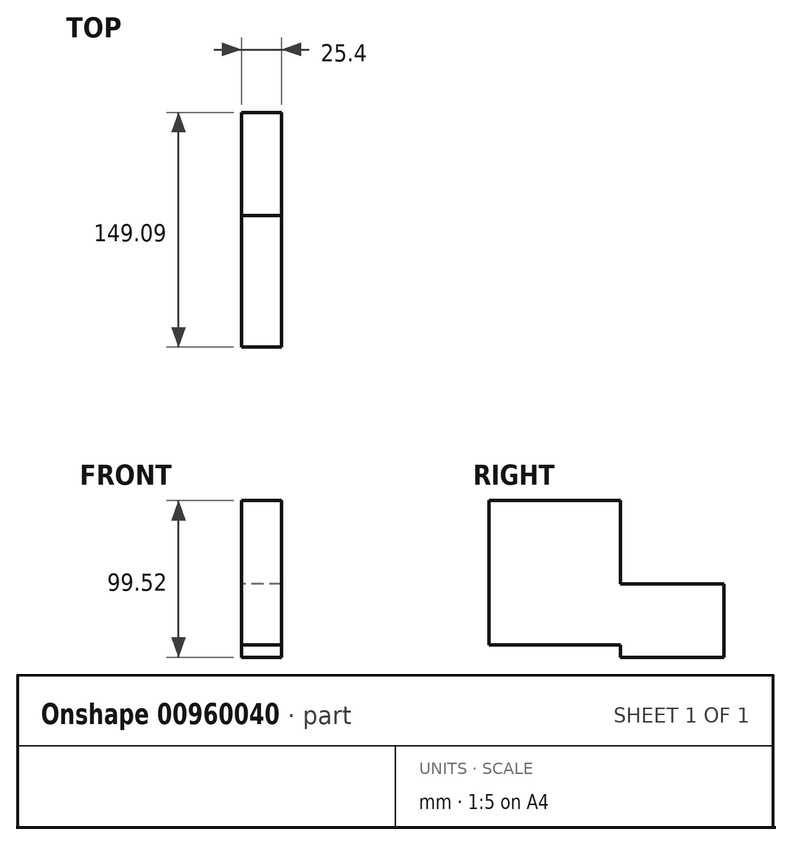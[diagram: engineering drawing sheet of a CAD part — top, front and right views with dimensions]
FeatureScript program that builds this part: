
annotation { "Feature Type Name" : "Feature", "Feature Type Description" : "" }
export const myFeature = defineFeature(function(context is Context, id is Id, definition is map)
    precondition{}
    {
        {
            var Q0;
            Q0=qCreatedBy(makeId("Right.planeOp"),FACE);
            var sketch = newSketch(context, id + "F0", { "sketchPlane" : qUnion([Q0])});
            skLineSegment(sketch, "E0.bottom", {"start": v(-48.48, 52.83) * mm, "end": v(34.93, 52.83) * mm});
            skLineSegment(sketch, "E0.top", {"start": v(-48.48, -38.83) * mm, "end": v(34.93, -38.83) * mm});
            skLineSegment(sketch, "E0.left", {"start": v(-48.48, 52.83) * mm, "end": v(-48.48, -38.83) * mm});
            skLineSegment(sketch, "E0.right", {"start": v(34.93, 52.83) * mm, "end": v(34.93, -38.83) * mm});
            skLineSegment(sketch, "E1.bottom", {"start": v(34.93, 0) * mm, "end": v(100.61, 0) * mm});
            skLineSegment(sketch, "E1.top", {"start": v(34.93, -46.7) * mm, "end": v(100.61, -46.7) * mm});
            skLineSegment(sketch, "E1.left", {"start": v(34.93, 0) * mm, "end": v(34.93, -46.7) * mm});
            skLineSegment(sketch, "E1.right", {"start": v(100.61, 0) * mm, "end": v(100.61, -46.7) * mm});
            skSolve(sketch);
        }
        {
            var Q0;
            Q0 = qSketchRegion(id + "F0", true);
            extrude(context, id + "F1", {"entities" : qUnion([Q0]), "depth" : 25.4 * mm, "offsetDistance" : 25.4 * mm});
        }
    });
